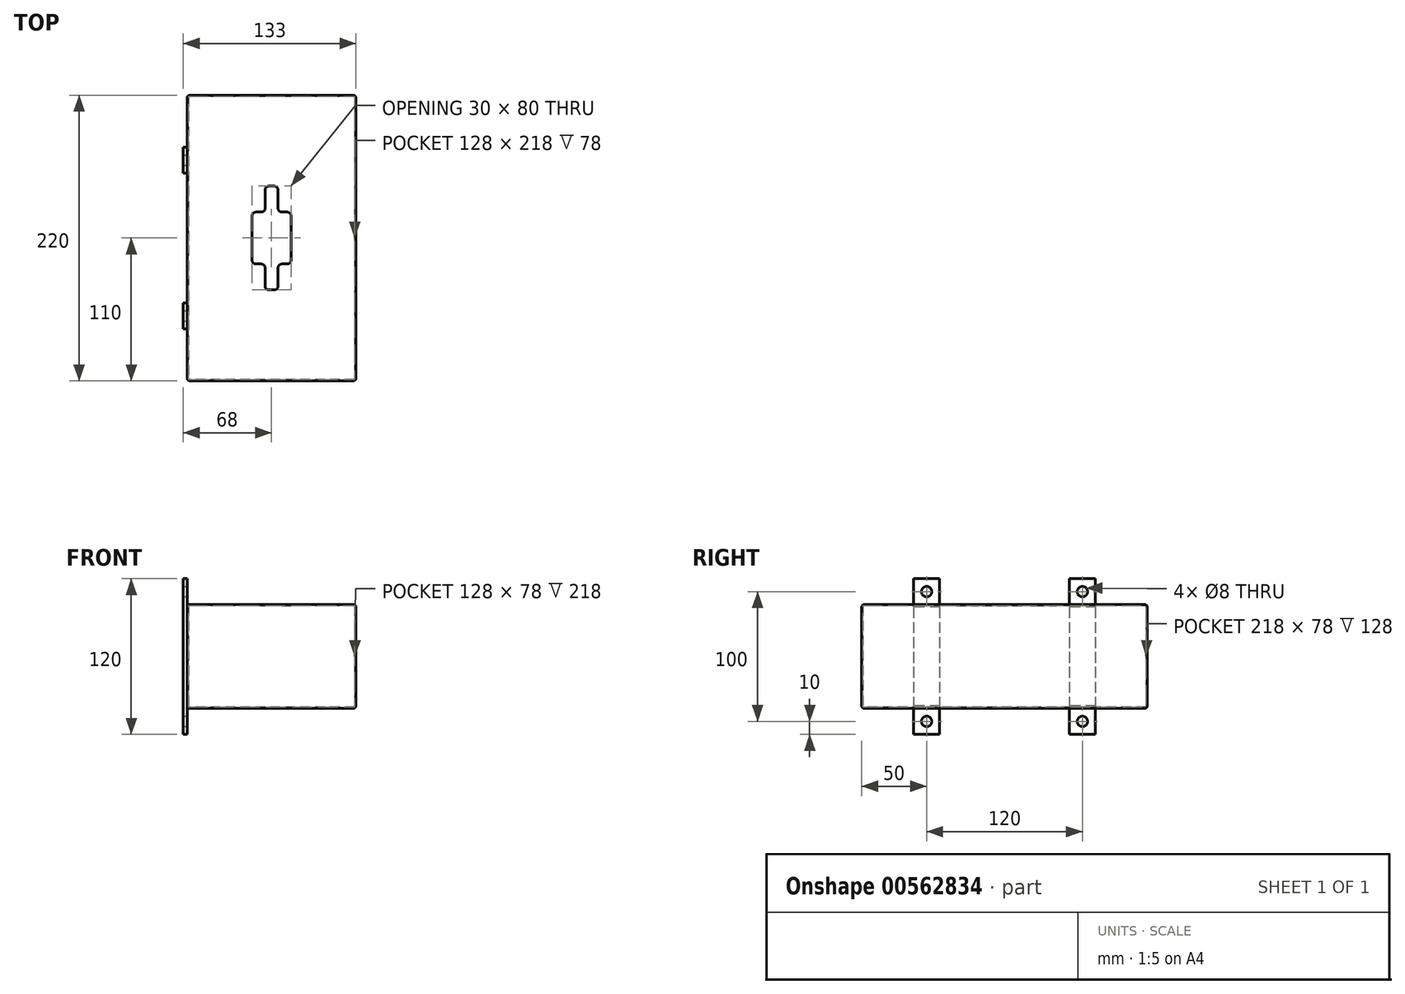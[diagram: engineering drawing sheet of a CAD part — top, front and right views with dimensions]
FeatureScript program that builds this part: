
annotation { "Feature Type Name" : "Feature", "Feature Type Description" : "" }
export const myFeature = defineFeature(function(context is Context, id is Id, definition is map)
    precondition{}
    {
        {
            var Q0;
            Q0=qCreatedBy(makeId("Top.planeOp"),FACE);
            var sketch = newSketch(context, id + "F0", { "sketchPlane" : qUnion([Q0])});
            skLineSegment(sketch, "E0.bottom", {"start": v(65, 110) * mm, "end": v(-65, 110) * mm});
            skLineSegment(sketch, "E0.top", {"start": v(65, -110) * mm, "end": v(-65, -110) * mm});
            skLineSegment(sketch, "E0.left", {"start": v(65, 110) * mm, "end": v(65, -110) * mm});
            skLineSegment(sketch, "E0.right", {"start": v(-65, 110) * mm, "end": v(-65, -110) * mm});
            skPoint(sketch, "E0.middle", {"position": v(0, 0) * mm});
            skSolve(sketch);
        }
        {
            var Q0;
            Q0=qSketchRegion(id+"F0",true);
            extrude(context, id + "F1", {"entities" : qUnion([Q0]), "endBound" : BoundingType.SYMMETRIC, "depth" : 80 * mm, "offsetDistance" : 25 * mm});
        }
        {
            var Q0;
            Q0=makeQuery(id+"F1.opExtrude","SWEPT_FACE",FACE,{"disambiguationData":[OSD([sQuery(id+"F0.wireOp",EDGE,"E0.left")])]});
            var Q1;
            Q1=makeQuery(id+"F1.opExtrude","SWEPT_FACE",FACE,{"disambiguationData":[OSD([sQuery(id+"F0.wireOp",EDGE,"E0.top")])]});
            var Q2;
            Q2=makeQuery(id+"F1.opExtrude","CAP_FACE",FACE,{"disambiguationData":[OSD([sQuery(id+"F0.wireOp",EDGE,"E0.bottom"),sQuery(id+"F0.wireOp",EDGE,"E0.top"),sQuery(id+"F0.wireOp",EDGE,"E0.left"),sQuery(id+"F0.wireOp",EDGE,"E0.right")])],"isStart":false});
            var Q3;
            Q3=makeQuery(id+"F1.opExtrude","SWEPT_FACE",FACE,{"disambiguationData":[OSD([sQuery(id+"F0.wireOp",EDGE,"E0.right")])]});
            var Q4;
            Q4=makeQuery(id+"F1.opExtrude","SWEPT_BODY",BODY,{"disambiguationData":[OSD([sQuery(id+"F0.wireOp",EDGE,"E0.bottom"),sQuery(id+"F0.wireOp",EDGE,"E0.top"),sQuery(id+"F0.wireOp",EDGE,"E0.left"),sQuery(id+"F0.wireOp",EDGE,"E0.right")])]});
            shell(context, id + "F2", {"isHollow" : true, "entities" : qUnion([Q0, Q1, Q2, Q3]), "parts" : qUnion([Q4]), "thickness" : 1 * mm});
        }
        {
            var Q0;
            Q0=makeQuery(id+"F1.opExtrude","CAP_FACE",FACE,{"disambiguationData":[OSD([sQuery(id+"F0.wireOp",EDGE,"E0.bottom"),sQuery(id+"F0.wireOp",EDGE,"E0.top"),sQuery(id+"F0.wireOp",EDGE,"E0.left"),sQuery(id+"F0.wireOp",EDGE,"E0.right")])],"isStart":false});
            var sketch = newSketch(context, id + "F3", { "sketchPlane" : qUnion([Q0])});
            skPoint(sketch, "E1.orphan", {"position": v(58.75, -193.86) * mm});
            skLineSegment(sketch, "E2.bottom", {"start": v(-2, 40) * mm, "end": v(2, 40) * mm});
            skLineSegment(sketch, "E2.top", {"start": v(-2, -40) * mm, "end": v(2, -40) * mm});
            skLineSegment(sketch, "E2.left", {"start": v(-5, 37) * mm, "end": v(-5, 23) * mm});
            skLineSegment(sketch, "E2.right", {"start": v(5, 37) * mm, "end": v(5, 23) * mm});
            skPoint(sketch, "E2.middle", {"position": v(0, 0) * mm});
            skLineSegment(sketch, "E3.bottom", {"start": v(-12, 20) * mm, "end": v(-8, 20) * mm});
            skLineSegment(sketch, "E3.top", {"start": v(-12, -20) * mm, "end": v(-8, -20) * mm});
            skLineSegment(sketch, "E3.left", {"start": v(-15, 17) * mm, "end": v(-15, -17) * mm});
            skPoint(sketch, "E3.middle", {"position": v(-5, 0) * mm});
            skLineSegment(sketch, "E4.bottom", {"start": v(12, 20) * mm, "end": v(8, 20) * mm});
            skLineSegment(sketch, "E4.top", {"start": v(12, -20) * mm, "end": v(8, -20) * mm});
            skLineSegment(sketch, "E4.left", {"start": v(15, 17) * mm, "end": v(15, -17) * mm});
            skPoint(sketch, "E4.middle", {"position": v(5, 0) * mm});
            skPoint(sketch, "E3.right.start.orphan", {"position": v(5, 20) * mm});
            skPoint(sketch, "E5.orphan", {"position": v(5, -20) * mm});
            skLineSegment(sketch, "E6.trimOffspring", {"start": v(-5, -23) * mm, "end": v(-5, -37) * mm});
            skLineSegment(sketch, "E7.trimOffspring", {"start": v(5, -23) * mm, "end": v(5, -37) * mm});
            skPoint(sketch, "E8.visualSharp", {"position": v(-15, 20) * mm});
            skArc(sketch, "E8.filletArc", {"start": v(-12, 20) * mm, "mid": v(-14.12, 19.12) * mm, "end": v(-15, 17) * mm});
            skPoint(sketch, "E9.visualSharp", {"position": v(-5, 20) * mm});
            skArc(sketch, "E9.filletArc", {"start": v(-8, 20) * mm, "mid": v(-5.88, 20.88) * mm, "end": v(-5, 23) * mm});
            skArc(sketch, "E10.filletArc", {"start": v(5, 23) * mm, "mid": v(5.88, 20.88) * mm, "end": v(8, 20) * mm});
            skPoint(sketch, "E11.visualSharp", {"position": v(15, 20) * mm});
            skArc(sketch, "E11.filletArc", {"start": v(15, 17) * mm, "mid": v(14.12, 19.12) * mm, "end": v(12, 20) * mm});
            skPoint(sketch, "E12.visualSharp", {"position": v(15, -20) * mm});
            skArc(sketch, "E12.filletArc", {"start": v(12, -20) * mm, "mid": v(14.12, -19.12) * mm, "end": v(15, -17) * mm});
            skArc(sketch, "E13.filletArc", {"start": v(8, -20) * mm, "mid": v(5.88, -20.88) * mm, "end": v(5, -23) * mm});
            skPoint(sketch, "E14.visualSharp", {"position": v(-5, -20) * mm});
            skArc(sketch, "E14.filletArc", {"start": v(-5, -23) * mm, "mid": v(-5.88, -20.88) * mm, "end": v(-8, -20) * mm});
            skPoint(sketch, "E15.visualSharp", {"position": v(-15, -20) * mm});
            skArc(sketch, "E15.filletArc", {"start": v(-15, -17) * mm, "mid": v(-14.12, -19.12) * mm, "end": v(-12, -20) * mm});
            skPoint(sketch, "E16.visualSharp", {"position": v(5, 40) * mm});
            skArc(sketch, "E16.filletArc", {"start": v(5, 37) * mm, "mid": v(4.12, 39.12) * mm, "end": v(2, 40) * mm});
            skPoint(sketch, "E17.visualSharp", {"position": v(-5, 40) * mm});
            skArc(sketch, "E17.filletArc", {"start": v(-2, 40) * mm, "mid": v(-4.12, 39.12) * mm, "end": v(-5, 37) * mm});
            skPoint(sketch, "E18.visualSharp", {"position": v(5, -40) * mm});
            skArc(sketch, "E18.filletArc", {"start": v(2, -40) * mm, "mid": v(4.12, -39.12) * mm, "end": v(5, -37) * mm});
            skPoint(sketch, "E19.visualSharp", {"position": v(-5, -40) * mm});
            skArc(sketch, "E19.filletArc", {"start": v(-5, -37) * mm, "mid": v(-4.12, -39.12) * mm, "end": v(-2, -40) * mm});
            skSolve(sketch);
        }
        {
            var Q0;
            Q0=qSketchRegion(id+"F3",true);
            extrude(context, id + "F4", {"entities" : qUnion([Q0]), "operationType" : NewBodyOperationType.REMOVE, "endBound" : BoundingType.UP_TO_NEXT, "oppositeDirection" : true, "depth" : 440 * mm, "offsetDistance" : 25 * mm});
        }
        {
            var Q0;
            Q0=makeQuery(id+"F1.opExtrude","SWEPT_FACE",FACE,{"disambiguationData":[OSD([sQuery(id+"F0.wireOp",EDGE,"E0.left")])]});
            var Q1;
            Q1=makeQuery(id+"F1.opExtrude","SWEPT_FACE",FACE,{"disambiguationData":[OSD([sQuery(id+"F0.wireOp",EDGE,"E0.right")])]});
            var Q2;
            Q2=makeQuery(id+"F1.opExtrude","CAP_FACE",FACE,{"disambiguationData":[OSD([sQuery(id+"F0.wireOp",EDGE,"E0.bottom"),sQuery(id+"F0.wireOp",EDGE,"E0.top"),sQuery(id+"F0.wireOp",EDGE,"E0.left"),sQuery(id+"F0.wireOp",EDGE,"E0.right")])],"isStart":true});
            var Q3;
            Q3=makeQuery(id+"F1.opExtrude","SWEPT_FACE",FACE,{"disambiguationData":[OSD([sQuery(id+"F0.wireOp",EDGE,"E0.bottom")])]});
            var Q4;
            Q4=makeQuery(id+"F1.opExtrude","CAP_EDGE",EDGE,{"disambiguationData":[OSD([sQuery(id+"F0.wireOp",EDGE,"E0.top")])],"isStart":false});
            fillet(context, id + "F5", {"entities" : qUnion([Q0, Q1, Q2, Q3, Q4]), "radius" : 2 * mm, "tangentPropagation" : true, "allowEdgeOverflow" : false});
        }
        {
            var Q0;
            Q0=makeQuery(id+"F1.opExtrude","SWEPT_FACE",FACE,{"disambiguationData":[OSD([sQuery(id+"F0.wireOp",EDGE,"E0.right")])]});
            var sketch = newSketch(context, id + "F6", { "sketchPlane" : qUnion([Q0])});
            skLineSegment(sketch, "E20.bottom", {"start": v(-70, 60) * mm, "end": v(-50, 60) * mm});
            skLineSegment(sketch, "E20.top", {"start": v(-70, -60) * mm, "end": v(-50, -60) * mm});
            skLineSegment(sketch, "E20.left", {"start": v(-70, 60) * mm, "end": v(-70, -60) * mm});
            skLineSegment(sketch, "E20.right", {"start": v(-50, 60) * mm, "end": v(-50, -60) * mm});
            skLineSegment(sketch, "E21.bottom", {"start": v(50, 60) * mm, "end": v(70, 60) * mm});
            skLineSegment(sketch, "E21.top", {"start": v(50, -60) * mm, "end": v(70, -60) * mm});
            skLineSegment(sketch, "E21.left", {"start": v(50, 60) * mm, "end": v(50, -60) * mm});
            skLineSegment(sketch, "E21.right", {"start": v(70, 60) * mm, "end": v(70, -60) * mm});
            skCircle(sketch, "E22", {"center": v(-60, 50) * mm, "radius": 4 * mm});
            skPoint(sketch, "E22.centerSnap0", {"position": v(-60, 60) * mm});
            skCircle(sketch, "E23", {"center": v(-60, -50) * mm, "radius": 4 * mm});
            skPoint(sketch, "E23.centerSnap0", {"position": v(-60, -60) * mm});
            skCircle(sketch, "E24.MirrorC", {"center": v(60, 50) * mm, "radius": 4 * mm});
            skCircle(sketch, "E25.MirrorC", {"center": v(60, -50) * mm, "radius": 4 * mm});
            skSolve(sketch);
        }
        {
            var Q0;
            Q0 = qSketchRegion(id + "F6", true);
            extrude(context, id + "F7", {"entities" : qUnion([Q0]), "operationType" : NewBodyOperationType.ADD, "depth" : 3 * mm, "offsetDistance" : 25 * mm});
        }
    });
